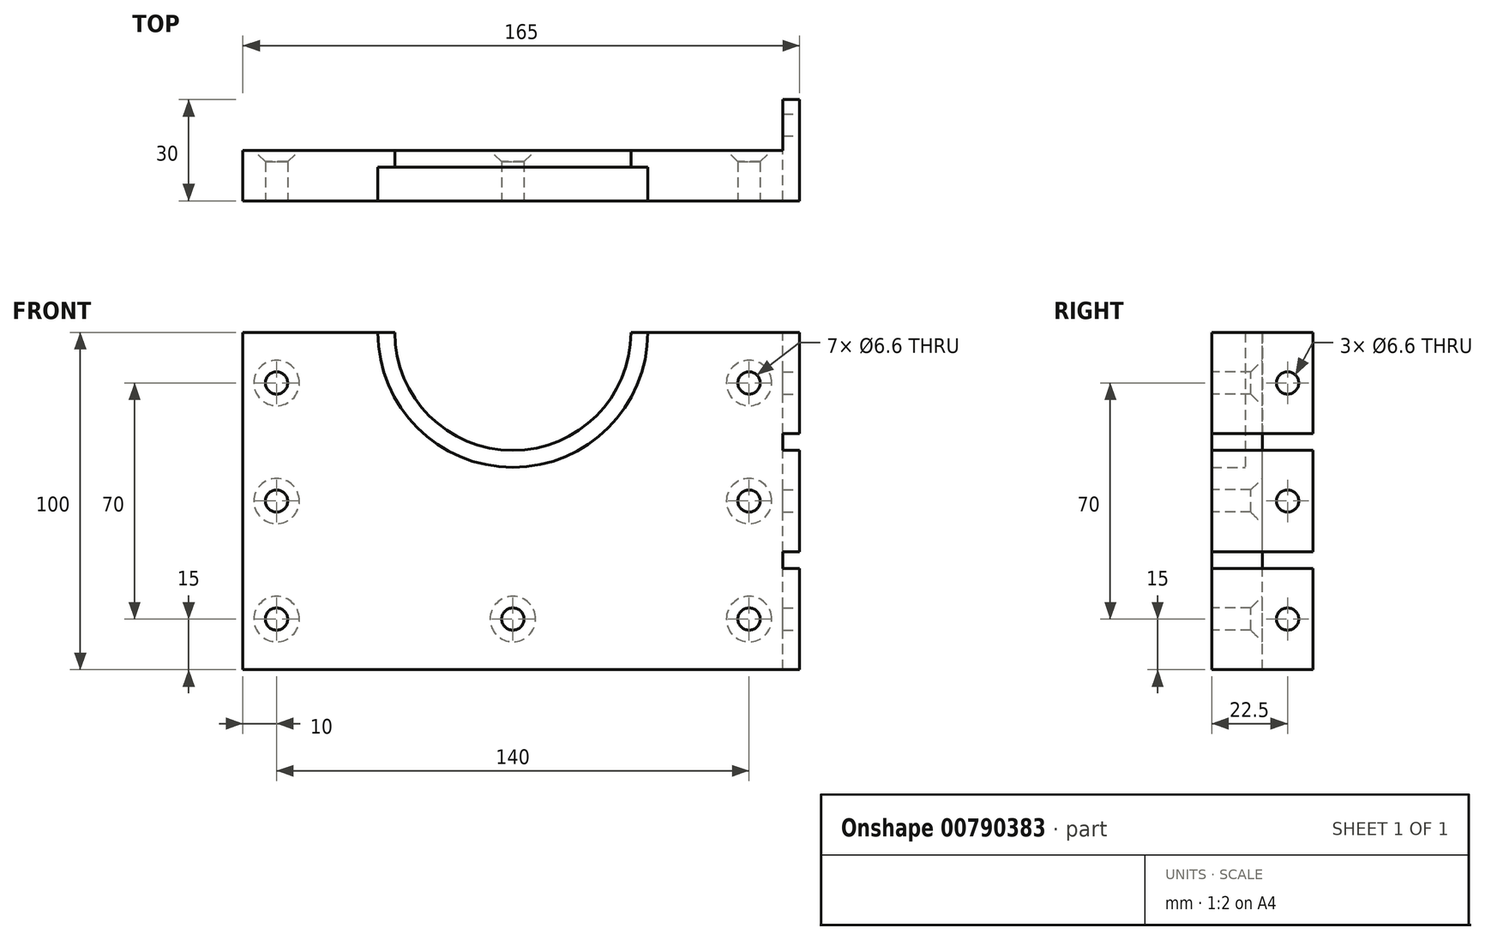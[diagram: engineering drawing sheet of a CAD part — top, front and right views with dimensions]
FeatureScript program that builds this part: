
annotation { "Feature Type Name" : "Feature", "Feature Type Description" : "" }
export const myFeature = defineFeature(function(context is Context, id is Id, definition is map)
    precondition{}
    {
        {
            var Q0;
            Q0=qCreatedBy(makeId("Front.planeOp"),FACE);
            var sketch = newSketch(context, id + "F0", { "sketchPlane" : qUnion([Q0])});
            skArc(sketch, "E0", {"start": v(-40, 40) * mm, "mid": v(0, 0) * mm, "end": v(40, 40) * mm});
            skLineSegment(sketch, "E1.top", {"start": v(80, 40) * mm, "end": v(40, 40) * mm});
            skLineSegment(sketch, "E1.left", {"start": v(80, -60) * mm, "end": v(80, 40) * mm});
            skLineSegment(sketch, "E1.right", {"start": v(-80, -60) * mm, "end": v(-80, 40) * mm});
            skPoint(sketch, "E1.middle", {"position": v(0, 0) * mm});
            skLineSegment(sketch, "E2.trimOffspring", {"start": v(-40, 40) * mm, "end": v(-80, 40) * mm});
            skLineSegment(sketch, "E3", {"start": v(-80, -60) * mm, "end": v(80, -60) * mm});
            skPoint(sketch, "E4", {"position": v(-70, 25) * mm});
            skPoint(sketch, "E5", {"position": v(70, 25) * mm});
            skPoint(sketch, "E6", {"position": v(70, -10) * mm});
            skPoint(sketch, "E7", {"position": v(-70, -10) * mm});
            skPoint(sketch, "E8", {"position": v(-70, -45) * mm});
            skPoint(sketch, "E9", {"position": v(70, -45) * mm});
            skPoint(sketch, "E10", {"position": v(0, -45) * mm});
            skSolve(sketch);
        }
        {
            var Q0;
            Q0=makeQuery(id+"F0.imprint","IMPRINT",FACE,{"disambiguationData":[TD([[makeQuery(id+"F0.imprint","IMPRINT",EDGE,{"derivedFrom":sQuery(id+"F0.wireOp",EDGE,"E0")}),-1.0]])]});
            extrude(context, id + "F1", {"entities" : qUnion([Q0]), "depth" : 10 * mm, "offsetDistance" : 25 * mm});
        }
        {
            var Q0;
            Q0=makeQuery(id+"F1.opExtrude","CAP_FACE",FACE,{"disambiguationData":[OSD([sQuery(id+"F0.wireOp",EDGE,"E0"),sQuery(id+"F0.wireOp",EDGE,"E1.top"),sQuery(id+"F0.wireOp",EDGE,"E1.left"),sQuery(id+"F0.wireOp",EDGE,"E1.right"),sQuery(id+"F0.wireOp",EDGE,"E2.trimOffspring"),sQuery(id+"F0.wireOp",EDGE,"E3")])],"isStart":true});
            var sketch = newSketch(context, id + "F2", { "sketchPlane" : qUnion([Q0])});
            skArc(sketch, "E11", {"start": v(-35, 40) * mm, "mid": v(0, 5) * mm, "end": v(35, 40) * mm});
            skLineSegment(sketch, "E12", {"start": v(-40, 40) * mm, "end": v(40, 40) * mm, "construction": true});
            skLineSegment(sketch, "E13", {"start": v(-40, 40) * mm, "end": v(-35, 40) * mm});
            skLineSegment(sketch, "E14", {"start": v(40, 40) * mm, "end": v(35, 40) * mm});
            skSolve(sketch);
        }
        {
            var Q0;
            {var subQ5=sQuery(id+"F0.wireOp",EDGE,"E0");Q0=makeQuery(id+"F2.imprint","IMPRINT",FACE,{"disambiguationData":[TD([[makeQuery(id+"F2.imprint","IMPRINT",EDGE,{"derivedFrom":makeQuery(id+"F1.opExtrude","CAP_EDGE",EDGE,{"disambiguationData":[OSD([subQ5])],"isStart":true})}),1.0]])]});}
            var Q1;
            Q1=makeQuery(id+"F2.imprint","IMPRINT",FACE,{"disambiguationData":[TD([[makeQuery(id+"F2.imprint","IMPRINT",EDGE,{"derivedFrom":sQuery(id+"F2.wireOp",EDGE,"E11")}),-1.0]])]});
            extrude(context, id + "F3", {"entities" : qUnion([Q0, Q1]), "operationType" : NewBodyOperationType.ADD, "depth" : 5 * mm, "offsetDistance" : 25 * mm});
        }
        {
            var Q0;
            {var subQ0=sQuery(id+"F0.wireOp",EDGE,"E1.left");Q0=makeQuery(id+"F3.boolean.opBoolean","MERGE",FACE,{"derivedFrom":[makeQuery(id+"F1.opExtrude","SWEPT_FACE",FACE,{"disambiguationData":[OSD([subQ0])]}),makeQuery(id+"F3.opExtrude","SWEPT_FACE",FACE,{"disambiguationData":[OSD([subQ0])]})]});}
            var sketch = newSketch(context, id + "F4", { "sketchPlane" : qUnion([Q0])});
            skLineSegment(sketch, "E15.bottom", {"start": v(-10, 40) * mm, "end": v(20, 40) * mm});
            skLineSegment(sketch, "E15.top", {"start": v(-10, 10) * mm, "end": v(20, 10) * mm});
            skLineSegment(sketch, "E15.left", {"start": v(-10, 40) * mm, "end": v(-10, 10) * mm});
            skLineSegment(sketch, "E15.right", {"start": v(20, 40) * mm, "end": v(20, 10) * mm});
            skLineSegment(sketch, "E16.bottom", {"start": v(-10, 5) * mm, "end": v(20, 5) * mm});
            skLineSegment(sketch, "E16.top", {"start": v(-10, -25) * mm, "end": v(20, -25) * mm});
            skLineSegment(sketch, "E16.left", {"start": v(-10, 5) * mm, "end": v(-10, -25) * mm});
            skLineSegment(sketch, "E16.right", {"start": v(20, 5) * mm, "end": v(20, -25) * mm});
            skLineSegment(sketch, "E17.bottom", {"start": v(-10, -30) * mm, "end": v(20, -30) * mm});
            skLineSegment(sketch, "E17.top", {"start": v(-10, -60) * mm, "end": v(20, -60) * mm});
            skLineSegment(sketch, "E17.left", {"start": v(-10, -30) * mm, "end": v(-10, -60) * mm});
            skLineSegment(sketch, "E17.right", {"start": v(20, -30) * mm, "end": v(20, -60) * mm});
            skPoint(sketch, "E18", {"position": v(20, 25) * mm});
            skPoint(sketch, "E19", {"position": v(20, -10) * mm});
            skPoint(sketch, "E20", {"position": v(20, -45) * mm});
            skPoint(sketch, "E21", {"position": v(12.5, 25) * mm});
            skPoint(sketch, "E22", {"position": v(12.5, -10) * mm});
            skPoint(sketch, "E23", {"position": v(12.5, -45) * mm});
            skSolve(sketch);
        }
        {
            var Q0;
            {var subQ0=sQuery(id+"F4.wireOp",EDGE,"E15.left");Q0=makeQuery(id+"F4.imprint","IMPRINT",FACE,{"disambiguationData":[TD([[makeQuery(id+"F4.imprint","IMPRINT",EDGE,{"derivedFrom":subQ0}),-1.0]])]});}
            var Q1;
            {var subQ3=sQuery(id+"F4.wireOp",EDGE,"E15.right");Q1=makeQuery(id+"F4.imprint","IMPRINT",FACE,{"disambiguationData":[TD([[makeQuery(id+"F4.imprint","IMPRINT",EDGE,{"derivedFrom":subQ3}),-1.0]])]});}
            var Q2;
            {var subQ0=sQuery(id+"F4.wireOp",EDGE,"E16.left");Q2=makeQuery(id+"F4.imprint","IMPRINT",FACE,{"disambiguationData":[TD([[makeQuery(id+"F4.imprint","IMPRINT",EDGE,{"derivedFrom":subQ0}),-1.0]])]});}
            var Q3;
            {var subQ0=sQuery(id+"F4.wireOp",EDGE,"E16.right");Q3=makeQuery(id+"F4.imprint","IMPRINT",FACE,{"disambiguationData":[TD([[makeQuery(id+"F4.imprint","IMPRINT",EDGE,{"derivedFrom":subQ0}),-1.0]])]});}
            var Q4;
            {var subQ0=sQuery(id+"F4.wireOp",EDGE,"E17.right");Q4=makeQuery(id+"F4.imprint","IMPRINT",FACE,{"disambiguationData":[TD([[makeQuery(id+"F4.imprint","IMPRINT",EDGE,{"derivedFrom":subQ0}),-1.0]])]});}
            var Q5;
            {var subQ0=sQuery(id+"F4.wireOp",EDGE,"E17.left");Q5=makeQuery(id+"F4.imprint","IMPRINT",FACE,{"disambiguationData":[TD([[makeQuery(id+"F4.imprint","IMPRINT",EDGE,{"derivedFrom":subQ0}),-1.0]])]});}
            extrude(context, id + "F5", {"entities" : qUnion([Q0, Q1, Q2, Q3, Q4, Q5]), "operationType" : NewBodyOperationType.ADD, "depth" : 5 * mm, "offsetDistance" : 25 * mm});
        }
        {
            var Q0;
            Q0=sQuery(id+"F4.wireOp",VERTEX,"E21");
            var Q1;
            Q1=sQuery(id+"F4.wireOp",VERTEX,"E22");
            var Q2;
            Q2=sQuery(id+"F4.wireOp",VERTEX,"E23");
            var Q3;
            Q3=makeQuery(id+"F1.opExtrude","SWEPT_BODY",BODY,{"disambiguationData":[OSD([sQuery(id+"F0.wireOp",EDGE,"E0"),sQuery(id+"F0.wireOp",EDGE,"E1.top"),sQuery(id+"F0.wireOp",EDGE,"E1.left"),sQuery(id+"F0.wireOp",EDGE,"E1.right"),sQuery(id+"F0.wireOp",EDGE,"E2.trimOffspring"),sQuery(id+"F0.wireOp",EDGE,"E3")])]});
            hole(context, id + "F6", {"style" : HoleStyle.SIMPLE, "endStyle" : HoleEndStyle.BLIND, "oppositeDirection" : true, "standardTappedOrClearance" : lookupTablePath({ "standard" : "ISO", "fit" : "Normal", "size" : "M6", "type" : "Clearance" }), "standardBlindInLast" : lookupTablePath({ "fit" : "Standard", "standard" : "ISO", "size" : "M6", "type" : "Clearance" }), "holeDiameter" : 6.6 * mm, "majorDiameter" : 5 * mm, "holeDepth" : 14.25 * mm, "isTappedThrough" : true, "tappedDepth" : 11.25 * mm, "tapClearance" : 3, "startFromSketch" : true, "locations" : qUnion([Q0, Q1, Q2]), "scope" : qUnion([Q3])});
        }
        {
            var Q0;
            Q0=makeQuery(id+"F3.opExtrude","CAP_FACE",FACE,{"disambiguationData":[OSD([sQuery(id+"F0.wireOp",EDGE,"E1.top"),sQuery(id+"F0.wireOp",EDGE,"E1.left"),sQuery(id+"F0.wireOp",EDGE,"E1.right"),sQuery(id+"F0.wireOp",EDGE,"E2.trimOffspring"),sQuery(id+"F0.wireOp",EDGE,"E3"),sQuery(id+"F2.wireOp",EDGE,"E11"),sQuery(id+"F2.wireOp",EDGE,"E13"),sQuery(id+"F2.wireOp",EDGE,"E14")])],"isStart":false});
            var sketch = newSketch(context, id + "F7", { "sketchPlane" : qUnion([Q0])});
            skPoint(sketch, "E24", {"position": v(-70, 25) * mm});
            skPoint(sketch, "E25", {"position": v(-70, -10) * mm});
            skPoint(sketch, "E26", {"position": v(-70, -45) * mm});
            skPoint(sketch, "E27", {"position": v(0, -45) * mm});
            skPoint(sketch, "E28", {"position": v(70, -45) * mm});
            skPoint(sketch, "E29", {"position": v(70, -10) * mm});
            skPoint(sketch, "E30", {"position": v(70, 25) * mm});
            skSolve(sketch);
        }
        {
            var Q0;
            Q0=sQuery(id+"F7.wireOp",VERTEX,"E24");
            var Q1;
            Q1=sQuery(id+"F7.wireOp",VERTEX,"E25");
            var Q2;
            Q2=sQuery(id+"F7.wireOp",VERTEX,"E26");
            var Q3;
            Q3=sQuery(id+"F7.wireOp",VERTEX,"E27");
            var Q4;
            Q4=sQuery(id+"F7.wireOp",VERTEX,"E28");
            var Q5;
            Q5=sQuery(id+"F7.wireOp",VERTEX,"E29");
            var Q6;
            Q6=sQuery(id+"F7.wireOp",VERTEX,"E30");
            var Q7;
            Q7=makeQuery(id+"F1.opExtrude","SWEPT_BODY",BODY,{"disambiguationData":[OSD([sQuery(id+"F0.wireOp",EDGE,"E0"),sQuery(id+"F0.wireOp",EDGE,"E1.top"),sQuery(id+"F0.wireOp",EDGE,"E1.left"),sQuery(id+"F0.wireOp",EDGE,"E1.right"),sQuery(id+"F0.wireOp",EDGE,"E2.trimOffspring"),sQuery(id+"F0.wireOp",EDGE,"E3")])]});
            hole(context, id + "F8", {"style" : HoleStyle.C_SINK, "endStyle" : HoleEndStyle.THROUGH, "standardTappedOrClearance" : lookupTablePath({ "standard" : "ISO", "fit" : "Normal", "size" : "M6", "type" : "Clearance" }), "standardBlindInLast" : lookupTablePath({ "fit" : "Standard", "standard" : "ISO", "size" : "M6", "type" : "Clearance" }), "holeDiameter" : 6.6 * mm, "cSinkDiameter" : 13.44 * mm, "cSinkAngle" : 90 * degree, "majorDiameter" : 6 * mm, "isTappedThrough" : true, "tappedDepth" : 11.25 * mm, "tapClearance" : 3, "startFromSketch" : true, "locations" : qUnion([Q0, Q1, Q2, Q3, Q4, Q5, Q6]), "scope" : qUnion([Q7])});
        }
    });
